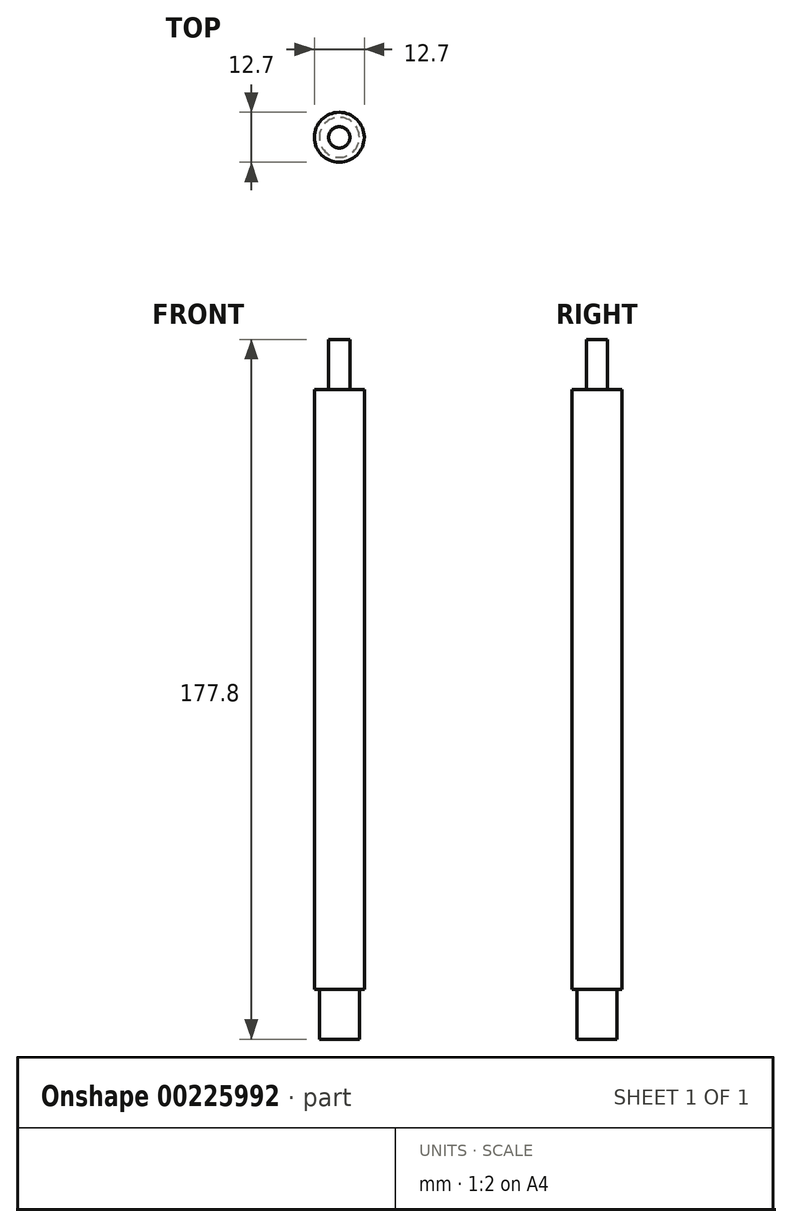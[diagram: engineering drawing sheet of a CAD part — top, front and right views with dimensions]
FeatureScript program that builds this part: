
annotation { "Feature Type Name" : "Feature", "Feature Type Description" : "" }
export const myFeature = defineFeature(function(context is Context, id is Id, definition is map)
    precondition{}
    {
        {
            var Q0;
            Q0=qCreatedBy(makeId("Top.planeOp"),FACE);
            var sketch = newSketch(context, id + "F0", { "sketchPlane" : qUnion([Q0])});
            skCircle(sketch, "E0", {"center": v(0, 0) * mm, "radius": 6.35 * mm});
            skSolve(sketch);
        }
        {
            var Q0;
            Q0 = qSketchRegion(id + "F0", true);
            extrude(context, id + "F1", {"entities" : qUnion([Q0]), "endBound" : BoundingType.SYMMETRIC, "depth" : 177.8 * mm});
        }
        {
            var Q0;
            Q0=makeQuery(id+"F1.opExtrude","CAP_FACE",FACE,{"disambiguationData":[OSD([sQuery(id+"F0.wireOp",EDGE,"E0")])],"isStart":false});
            var sketch = newSketch(context, id + "F2", { "sketchPlane" : qUnion([Q0])});
            skCircle(sketch, "E1.0", {"center": v(0, 0) * mm, "radius": 6.35 * mm});
            skCircle(sketch, "E2", {"center": v(0, 0) * mm, "radius": 2.7 * mm});
            skSolve(sketch);
        }
        {
            var Q0;
            Q0 = qSketchRegion(id + "F2", true);
            extrude(context, id + "F3", {"entities" : qUnion([Q0]), "operationType" : NewBodyOperationType.REMOVE, "oppositeDirection" : true, "depth" : 12.7 * mm});
        }
        {
            var Q0;
            Q0=makeQuery(id+"F1.opExtrude","CAP_FACE",FACE,{"disambiguationData":[OSD([sQuery(id+"F0.wireOp",EDGE,"E0")])],"isStart":true});
            var sketch = newSketch(context, id + "F4", { "sketchPlane" : qUnion([Q0])});
            skCircle(sketch, "E3.0", {"center": v(0, 0) * mm, "radius": 6.35 * mm});
            skCircle(sketch, "E4", {"center": v(0, 0) * mm, "radius": 5.08 * mm});
            skSolve(sketch);
        }
        {
            var Q0;
            Q0 = qSketchRegion(id + "F4", true);
            extrude(context, id + "F5", {"entities" : qUnion([Q0]), "operationType" : NewBodyOperationType.REMOVE, "oppositeDirection" : true, "depth" : 12.7 * mm});
        }
    });
